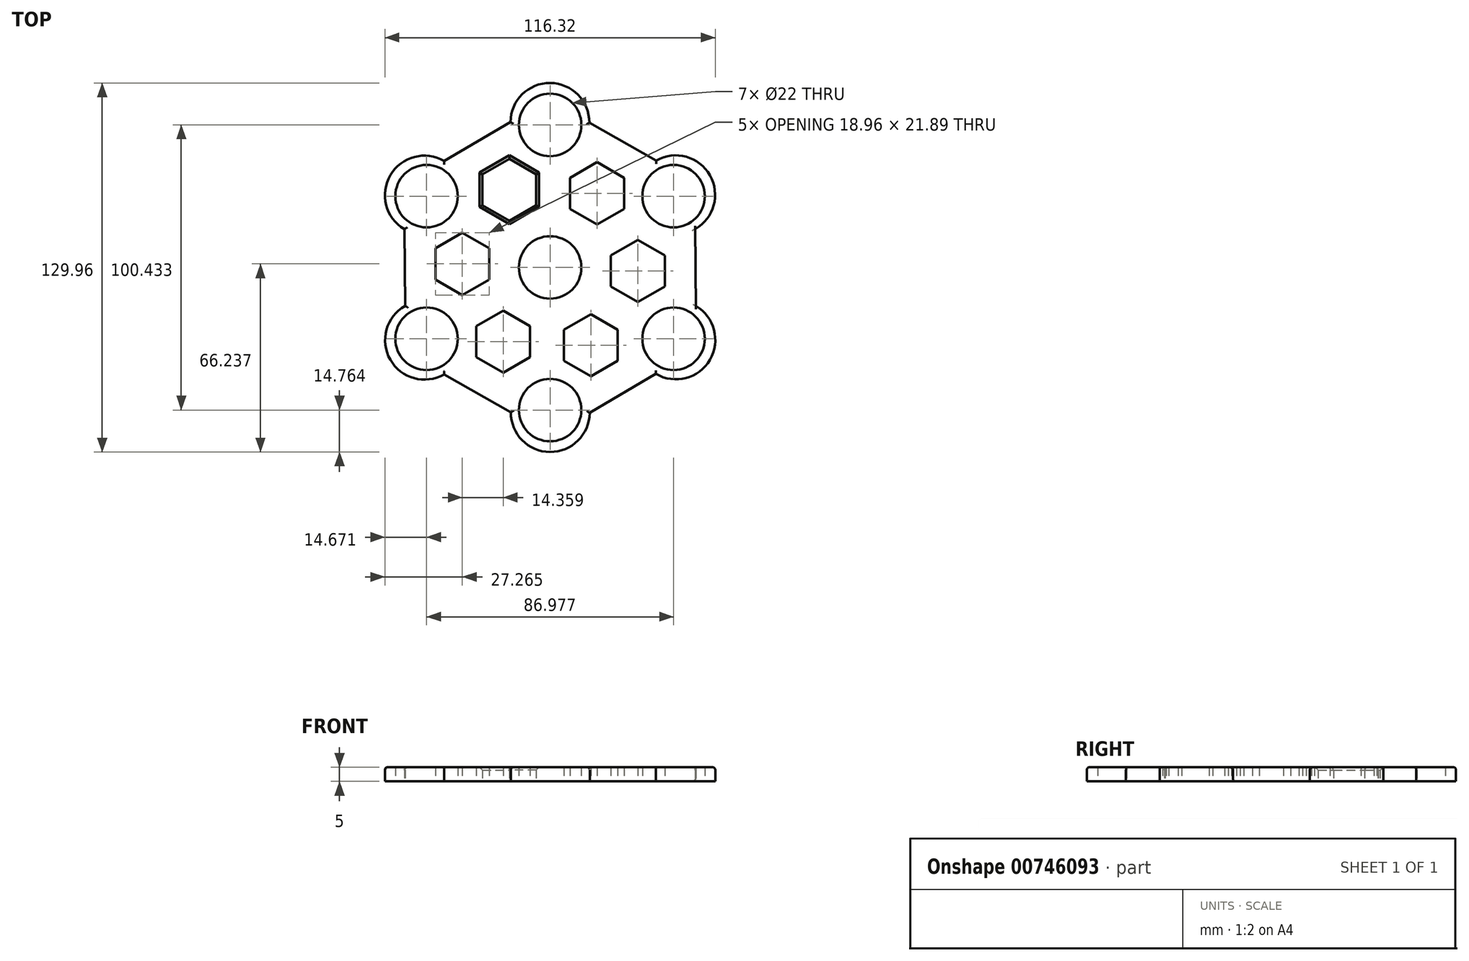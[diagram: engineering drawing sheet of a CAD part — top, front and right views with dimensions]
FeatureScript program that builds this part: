
annotation { "Feature Type Name" : "Feature", "Feature Type Description" : "" }
export const myFeature = defineFeature(function(context is Context, id is Id, definition is map)
    precondition{}
    {
        {
            var Q0;
            Q0=qCreatedBy(makeId("Top.planeOp"),FACE);
            var sketch = newSketch(context, id + "F0", { "sketchPlane" : qUnion([Q0])});
            skCircle(sketch, "E0", {"center": v(0, 0) * mm, "radius": 11 * mm});
            skCircle(sketch, "E1", {"center": v(0, 50.22) * mm, "radius": 11 * mm});
            skCircle(sketch, "E2.1.0", {"center": v(-43.49, 25.1) * mm, "radius": 11 * mm});
            skCircle(sketch, "E2.2.0", {"center": v(-43.49, -25.1) * mm, "radius": 11 * mm});
            skCircle(sketch, "E2.3.0", {"center": v(0, -50.22) * mm, "radius": 11 * mm});
            skCircle(sketch, "E2.4.0", {"center": v(43.49, -25.1) * mm, "radius": 11 * mm});
            skCircle(sketch, "E2.5.0", {"center": v(43.49, 25.1) * mm, "radius": 11 * mm});
            skArc(sketch, "E3", {"start": v(13.82, 51) * mm, "mid": v(0.03, 64.98) * mm, "end": v(-13.95, 51.19) * mm});
            skArc(sketch, "E4.1.0", {"start": v(-37.25, 37.47) * mm, "mid": v(-56.25, 32.52) * mm, "end": v(-51.3, 13.52) * mm});
            skArc(sketch, "E4.2.0", {"start": v(-51.07, -13.53) * mm, "mid": v(-56.29, -32.46) * mm, "end": v(-37.36, -37.67) * mm});
            skArc(sketch, "E4.3.0", {"start": v(-13.82, -51) * mm, "mid": v(-0.03, -64.98) * mm, "end": v(13.95, -51.19) * mm});
            skArc(sketch, "E4.4.0", {"start": v(37.25, -37.47) * mm, "mid": v(56.25, -32.52) * mm, "end": v(51.3, -13.52) * mm});
            skArc(sketch, "E4.5.0", {"start": v(51.07, 13.53) * mm, "mid": v(56.29, 32.46) * mm, "end": v(37.36, 37.67) * mm});
            skLineSegment(sketch, "E5", {"start": v(-37.25, 37.47) * mm, "end": v(-13.95, 51.19) * mm});
            skLineSegment(sketch, "E6.1.0", {"start": v(-51.07, -13.53) * mm, "end": v(-51.3, 13.52) * mm});
            skLineSegment(sketch, "E6.2.0", {"start": v(-13.82, -51) * mm, "end": v(-37.36, -37.67) * mm});
            skLineSegment(sketch, "E6.3.0", {"start": v(37.25, -37.47) * mm, "end": v(13.95, -51.19) * mm});
            skLineSegment(sketch, "E6.4.0", {"start": v(51.07, 13.53) * mm, "end": v(51.3, -13.52) * mm});
            skLineSegment(sketch, "E6.5.0", {"start": v(13.82, 51) * mm, "end": v(37.36, 37.67) * mm});
            skCircle(sketch, "E7.cCircle", {"center": v(-14.36, 27.38) * mm, "radius": 9.48 * mm, "construction": true});
            skLineSegment(sketch, "E7.0", {"start": v(-4.88, 32.86) * mm, "end": v(-4.88, 21.91) * mm});
            skLineSegment(sketch, "E7.1", {"start": v(-4.88, 21.91) * mm, "end": v(-14.36, 16.44) * mm});
            skLineSegment(sketch, "E7.2", {"start": v(-14.36, 16.44) * mm, "end": v(-23.84, 21.91) * mm});
            skLineSegment(sketch, "E7.3", {"start": v(-23.84, 21.91) * mm, "end": v(-23.84, 32.86) * mm});
            skLineSegment(sketch, "E7.4", {"start": v(-23.84, 32.86) * mm, "end": v(-14.36, 38.33) * mm});
            skLineSegment(sketch, "E7.5", {"start": v(-14.36, 38.33) * mm, "end": v(-4.88, 32.86) * mm});
            skPoint(sketch, "E7.0.midPoint", {"position": v(-4.88, 27.38) * mm});
            skLineSegment(sketch, "E8.1.0", {"start": v(-30.9, -9.69) * mm, "end": v(-40.38, -4.22) * mm});
            skLineSegment(sketch, "E8.1.1", {"start": v(-40.38, -4.22) * mm, "end": v(-40.38, 6.73) * mm});
            skCircle(sketch, "E8.1.2", {"center": v(-30.9, 1.26) * mm, "radius": 9.48 * mm, "construction": true});
            skLineSegment(sketch, "E8.1.3", {"start": v(-30.9, 12.2) * mm, "end": v(-21.41, 6.73) * mm});
            skLineSegment(sketch, "E8.1.4", {"start": v(-21.41, 6.73) * mm, "end": v(-21.41, -4.22) * mm});
            skLineSegment(sketch, "E8.1.5", {"start": v(-21.41, -4.22) * mm, "end": v(-30.9, -9.69) * mm});
            skLineSegment(sketch, "E8.1.6", {"start": v(-40.38, 6.73) * mm, "end": v(-30.9, 12.2) * mm});
            skLineSegment(sketch, "E8.2.0", {"start": v(-7.06, -31.6) * mm, "end": v(-16.54, -37.07) * mm});
            skLineSegment(sketch, "E8.2.1", {"start": v(-16.54, -37.07) * mm, "end": v(-26.02, -31.6) * mm});
            skCircle(sketch, "E8.2.2", {"center": v(-16.54, -26.13) * mm, "radius": 9.48 * mm, "construction": true});
            skLineSegment(sketch, "E8.2.3", {"start": v(-26.02, -20.65) * mm, "end": v(-16.54, -15.18) * mm});
            skLineSegment(sketch, "E8.2.4", {"start": v(-16.54, -15.18) * mm, "end": v(-7.06, -20.65) * mm});
            skLineSegment(sketch, "E8.2.5", {"start": v(-7.06, -20.65) * mm, "end": v(-7.06, -31.6) * mm});
            skLineSegment(sketch, "E8.2.6", {"start": v(-26.02, -31.6) * mm, "end": v(-26.02, -20.65) * mm});
            skLineSegment(sketch, "E8.3.0", {"start": v(23.84, -21.91) * mm, "end": v(23.84, -32.86) * mm});
            skLineSegment(sketch, "E8.3.1", {"start": v(23.84, -32.86) * mm, "end": v(14.36, -38.33) * mm});
            skCircle(sketch, "E8.3.2", {"center": v(14.36, -27.38) * mm, "radius": 9.48 * mm, "construction": true});
            skLineSegment(sketch, "E8.3.3", {"start": v(4.88, -32.86) * mm, "end": v(4.88, -21.91) * mm});
            skLineSegment(sketch, "E8.3.4", {"start": v(4.88, -21.91) * mm, "end": v(14.36, -16.44) * mm});
            skLineSegment(sketch, "E8.3.5", {"start": v(14.36, -16.44) * mm, "end": v(23.84, -21.91) * mm});
            skLineSegment(sketch, "E8.3.6", {"start": v(14.36, -38.33) * mm, "end": v(4.88, -32.86) * mm});
            skLineSegment(sketch, "E8.4.0", {"start": v(30.9, 9.69) * mm, "end": v(40.38, 4.22) * mm});
            skLineSegment(sketch, "E8.4.1", {"start": v(40.38, 4.22) * mm, "end": v(40.38, -6.73) * mm});
            skCircle(sketch, "E8.4.2", {"center": v(30.9, -1.26) * mm, "radius": 9.48 * mm, "construction": true});
            skLineSegment(sketch, "E8.4.3", {"start": v(30.9, -12.2) * mm, "end": v(21.41, -6.73) * mm});
            skLineSegment(sketch, "E8.4.4", {"start": v(21.41, -6.73) * mm, "end": v(21.41, 4.22) * mm});
            skLineSegment(sketch, "E8.4.5", {"start": v(21.41, 4.22) * mm, "end": v(30.9, 9.69) * mm});
            skLineSegment(sketch, "E8.4.6", {"start": v(40.38, -6.73) * mm, "end": v(30.9, -12.2) * mm});
            skLineSegment(sketch, "E8.5.0", {"start": v(7.06, 31.6) * mm, "end": v(16.54, 37.07) * mm});
            skLineSegment(sketch, "E8.5.1", {"start": v(16.54, 37.07) * mm, "end": v(26.02, 31.6) * mm});
            skCircle(sketch, "E8.5.2", {"center": v(16.54, 26.13) * mm, "radius": 9.48 * mm, "construction": true});
            skLineSegment(sketch, "E8.5.3", {"start": v(26.02, 20.65) * mm, "end": v(16.54, 15.18) * mm});
            skLineSegment(sketch, "E8.5.4", {"start": v(16.54, 15.18) * mm, "end": v(7.06, 20.65) * mm});
            skLineSegment(sketch, "E8.5.5", {"start": v(7.06, 20.65) * mm, "end": v(7.06, 31.6) * mm});
            skLineSegment(sketch, "E8.5.6", {"start": v(26.02, 31.6) * mm, "end": v(26.02, 20.65) * mm});
            skSolve(sketch);
        }
        {
            var Q0;
            Q0=makeQuery(id+"F0.imprint","IMPRINT",FACE,{"disambiguationData":[TD([[makeQuery(id+"F0.imprint","IMPRINT",EDGE,{"derivedFrom":sQuery(id+"F0.wireOp",EDGE,"E0")}),-1.0]])]});
            extrude(context, id + "F1", {"entities" : qUnion([Q0]), "depth" : 5 * mm, "offsetDistance" : 25 * mm});
        }
        {
            var Q0;
            Q0=makeQuery(id+"F1.opExtrude","CAP_EDGE",EDGE,{"disambiguationData":[OSD([sQuery(id+"F0.wireOp",EDGE,"E6.2.0")])],"isStart":false});
            var Q1;
            Q1=makeQuery(id+"F1.opExtrude","CAP_EDGE",EDGE,{"disambiguationData":[OSD([sQuery(id+"F0.wireOp",EDGE,"E4.2.0")])],"isStart":false});
            var Q2;
            Q2=makeQuery(id+"F1.opExtrude","CAP_EDGE",EDGE,{"disambiguationData":[OSD([sQuery(id+"F0.wireOp",EDGE,"E6.1.0")])],"isStart":false});
            var Q3;
            Q3=makeQuery(id+"F1.opExtrude","CAP_EDGE",EDGE,{"disambiguationData":[OSD([sQuery(id+"F0.wireOp",EDGE,"E4.1.0")])],"isStart":false});
            var Q4;
            Q4=makeQuery(id+"F1.opExtrude","CAP_EDGE",EDGE,{"disambiguationData":[OSD([sQuery(id+"F0.wireOp",EDGE,"E5")])],"isStart":false});
            var Q5;
            Q5=makeQuery(id+"F1.opExtrude","CAP_EDGE",EDGE,{"disambiguationData":[OSD([sQuery(id+"F0.wireOp",EDGE,"E3")])],"isStart":false});
            var Q6;
            Q6=makeQuery(id+"F1.opExtrude","CAP_EDGE",EDGE,{"disambiguationData":[OSD([sQuery(id+"F0.wireOp",EDGE,"E6.5.0")])],"isStart":false});
            var Q7;
            Q7=makeQuery(id+"F1.opExtrude","CAP_EDGE",EDGE,{"disambiguationData":[OSD([sQuery(id+"F0.wireOp",EDGE,"E4.5.0")])],"isStart":false});
            var Q8;
            Q8=makeQuery(id+"F1.opExtrude","CAP_EDGE",EDGE,{"disambiguationData":[OSD([sQuery(id+"F0.wireOp",EDGE,"E6.4.0")])],"isStart":true});
            var Q9;
            Q9=makeQuery(id+"F1.opExtrude","CAP_EDGE",EDGE,{"disambiguationData":[OSD([sQuery(id+"F0.wireOp",EDGE,"E4.4.0")])],"isStart":false});
            var Q10;
            Q10=makeQuery(id+"F1.opExtrude","CAP_EDGE",EDGE,{"disambiguationData":[OSD([sQuery(id+"F0.wireOp",EDGE,"E6.3.0")])],"isStart":false});
            var Q11;
            Q11=makeQuery(id+"F1.opExtrude","CAP_EDGE",EDGE,{"disambiguationData":[OSD([sQuery(id+"F0.wireOp",EDGE,"E4.3.0")])],"isStart":false});
            fillet(context, id + "F2", {"entities" : qUnion([Q0, Q1, Q2, Q3, Q4, Q5, Q6, Q7, Q8, Q9, Q10, Q11]), "radius" : 1 * mm, "tangentPropagation" : true, "allowEdgeOverflow" : false});
        }
        {
            var Q0;
            Q0=makeQuery(id+"F1.opExtrude","CAP_EDGE",EDGE,{"disambiguationData":[OSD([sQuery(id+"F0.wireOp",EDGE,"E7.4")])],"isStart":false});
            var Q1;
            Q1=makeQuery(id+"F1.opExtrude","CAP_EDGE",EDGE,{"disambiguationData":[OSD([sQuery(id+"F0.wireOp",EDGE,"E7.5")])],"isStart":false});
            var Q2;
            Q2=makeQuery(id+"F1.opExtrude","CAP_EDGE",EDGE,{"disambiguationData":[OSD([sQuery(id+"F0.wireOp",EDGE,"E7.0")])],"isStart":false});
            var Q3;
            Q3=makeQuery(id+"F1.opExtrude","CAP_EDGE",EDGE,{"disambiguationData":[OSD([sQuery(id+"F0.wireOp",EDGE,"E7.1")])],"isStart":false});
            var Q4;
            Q4=makeQuery(id+"F1.opExtrude","CAP_EDGE",EDGE,{"disambiguationData":[OSD([sQuery(id+"F0.wireOp",EDGE,"E7.2")])],"isStart":false});
            var Q5;
            Q5=makeQuery(id+"F1.opExtrude","CAP_EDGE",EDGE,{"disambiguationData":[OSD([sQuery(id+"F0.wireOp",EDGE,"E7.3")])],"isStart":false});
            chamfer(context, id + "F3", {"entities" : qUnion([Q0, Q1, Q2, Q3, Q4, Q5]), "width" : 1 * mm, "tangentPropagation" : true});
        }
    });
